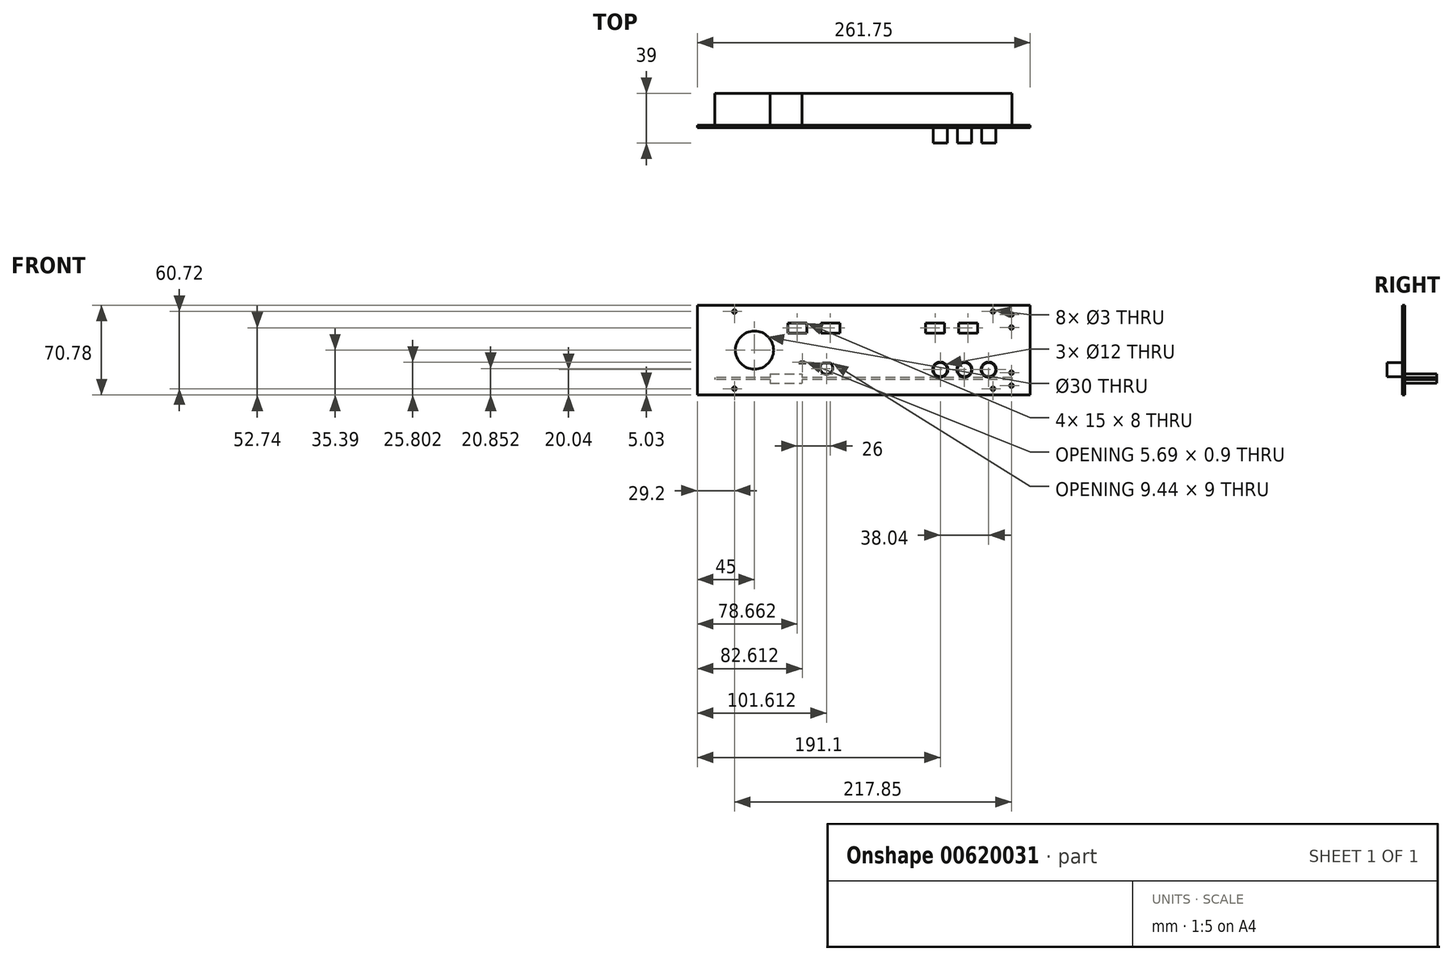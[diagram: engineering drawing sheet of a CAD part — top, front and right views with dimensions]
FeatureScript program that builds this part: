
annotation { "Feature Type Name" : "Feature", "Feature Type Description" : "" }
export const myFeature = defineFeature(function(context is Context, id is Id, definition is map)
    precondition{}
    {
        {
            var Q0;
            Q0=qCreatedBy(makeId("Front.planeOp"),FACE);
            var sketch = newSketch(context, id + "F0", { "sketchPlane" : qUnion([Q0])});
            skLineSegment(sketch, "E0.bottom", {"start": v(0, 0) * mm, "end": v(261.75, 0) * mm});
            skLineSegment(sketch, "E0.top", {"start": v(0, 70.78) * mm, "end": v(261.75, 70.78) * mm});
            skLineSegment(sketch, "E0.left", {"start": v(0, 0) * mm, "end": v(0, 70.78) * mm});
            skLineSegment(sketch, "E0.right", {"start": v(261.75, 0) * mm, "end": v(261.75, 70.78) * mm});
            skCircle(sketch, "E1", {"center": v(29.2, 5.03) * mm, "radius": 1.5 * mm});
            skCircle(sketch, "E2", {"center": v(29.2, 65.75) * mm, "radius": 1.5 * mm});
            skCircle(sketch, "E3", {"center": v(232.55, 65.75) * mm, "radius": 1.5 * mm});
            skCircle(sketch, "E4", {"center": v(232.55, 5.03) * mm, "radius": 1.5 * mm});
            skSolve(sketch);
        }
        {
            var Q0;
            Q0 = qSketchRegion(id + "F0", true);
            extrude(context, id + "F1", {"entities" : qUnion([Q0]), "oppositeDirection" : true, "depth" : 2 * mm, "offsetDistance" : 25 * mm});
        }
        {
            var Q0;
            Q0=makeQuery(id+"F1.opExtrude","CAP_FACE",FACE,{"disambiguationData":[OSD([sQuery(id+"F0.wireOp",EDGE,"E0.bottom"),sQuery(id+"F0.wireOp",EDGE,"E0.top"),sQuery(id+"F0.wireOp",EDGE,"E0.left"),sQuery(id+"F0.wireOp",EDGE,"E0.right"),sQuery(id+"F0.wireOp",EDGE,"E1"),sQuery(id+"F0.wireOp",EDGE,"E2"),sQuery(id+"F0.wireOp",EDGE,"E3"),sQuery(id+"F0.wireOp",EDGE,"E4")])],"isStart":false});
            var sketch = newSketch(context, id + "F2", { "sketchPlane" : qUnion([Q0])});
            skLineSegment(sketch, "E5.bottom", {"start": v(-247.63, 13.86) * mm, "end": v(-13.67, 13.86) * mm});
            skLineSegment(sketch, "E5.top", {"start": v(-247.63, 12.26) * mm, "end": v(-13.67, 12.26) * mm});
            skLineSegment(sketch, "E5.left", {"start": v(-247.63, 13.86) * mm, "end": v(-247.63, 12.26) * mm});
            skLineSegment(sketch, "E5.right", {"start": v(-13.67, 13.86) * mm, "end": v(-13.67, 12.26) * mm});
            skSolve(sketch);
        }
        {
            var Q0;
            Q0 = qSketchRegion(id + "F2", true);
            extrude(context, id + "F3", {"entities" : qUnion([Q0]), "operationType" : NewBodyOperationType.ADD, "depth" : 25 * mm, "offsetDistance" : 25 * mm});
        }
        {
            var Q0;
            Q0=makeQuery(id+"F1.opExtrude","CAP_FACE",FACE,{"disambiguationData":[OSD([sQuery(id+"F0.wireOp",EDGE,"E0.bottom"),sQuery(id+"F0.wireOp",EDGE,"E0.top"),sQuery(id+"F0.wireOp",EDGE,"E0.left"),sQuery(id+"F0.wireOp",EDGE,"E0.right"),sQuery(id+"F0.wireOp",EDGE,"E1"),sQuery(id+"F0.wireOp",EDGE,"E2"),sQuery(id+"F0.wireOp",EDGE,"E3"),sQuery(id+"F0.wireOp",EDGE,"E4")])],"isStart":false});
            var sketch = newSketch(context, id + "F4", { "sketchPlane" : qUnion([Q0])});
            skLineSegment(sketch, "E6.bottom", {"start": v(-57.2, 16.76) * mm, "end": v(-82.2, 16.76) * mm});
            skLineSegment(sketch, "E6.top", {"start": v(-57.2, 9.36) * mm, "end": v(-82.2, 9.36) * mm});
            skLineSegment(sketch, "E6.left", {"start": v(-57.2, 16.76) * mm, "end": v(-57.2, 9.36) * mm});
            skLineSegment(sketch, "E6.right", {"start": v(-82.2, 16.76) * mm, "end": v(-82.2, 9.36) * mm});
            skSolve(sketch);
        }
        {
            var Q0;
            Q0 = qSketchRegion(id + "F4", true);
            extrude(context, id + "F5", {"entities" : qUnion([Q0]), "operationType" : NewBodyOperationType.ADD, "depth" : 25 * mm, "offsetDistance" : 25 * mm});
        }
        {
            var Q0;
            Q0=makeQuery(id+"F1.opExtrude","CAP_FACE",FACE,{"disambiguationData":[OSD([sQuery(id+"F0.wireOp",EDGE,"E0.bottom"),sQuery(id+"F0.wireOp",EDGE,"E0.top"),sQuery(id+"F0.wireOp",EDGE,"E0.left"),sQuery(id+"F0.wireOp",EDGE,"E0.right"),sQuery(id+"F0.wireOp",EDGE,"E1"),sQuery(id+"F0.wireOp",EDGE,"E2"),sQuery(id+"F0.wireOp",EDGE,"E3"),sQuery(id+"F0.wireOp",EDGE,"E4")])],"isStart":false});
            var sketch = newSketch(context, id + "F6", { "sketchPlane" : qUnion([Q0])});
            skCircle(sketch, "E7", {"center": v(-229.14, 20.04) * mm, "radius": 6 * mm});
            skCircle(sketch, "E8", {"center": v(-210.12, 20.04) * mm, "radius": 6 * mm});
            skCircle(sketch, "E9", {"center": v(-191.1, 20.04) * mm, "radius": 6 * mm});
            skSolve(sketch);
        }
        {
            var Q0;
            Q0 = qSketchRegion(id + "F6", true);
            extrude(context, id + "F7", {"entities" : qUnion([Q0]), "operationType" : NewBodyOperationType.REMOVE, "oppositeDirection" : true, "depth" : 25 * mm, "offsetDistance" : 25 * mm});
        }
        {
            var Q0;
            Q0=makeQuery(id+"F1.opExtrude","CAP_FACE",FACE,{"disambiguationData":[OSD([sQuery(id+"F0.wireOp",EDGE,"E0.bottom"),sQuery(id+"F0.wireOp",EDGE,"E0.top"),sQuery(id+"F0.wireOp",EDGE,"E0.left"),sQuery(id+"F0.wireOp",EDGE,"E0.right"),sQuery(id+"F0.wireOp",EDGE,"E1"),sQuery(id+"F0.wireOp",EDGE,"E2"),sQuery(id+"F0.wireOp",EDGE,"E3"),sQuery(id+"F0.wireOp",EDGE,"E4")])],"isStart":false});
            var sketch = newSketch(context, id + "F8", { "sketchPlane" : qUnion([Q0])});
            skCircle(sketch, "E10", {"center": v(-229.14, 20.04) * mm, "radius": 5.5 * mm});
            skCircle(sketch, "E11", {"center": v(-210.12, 20.04) * mm, "radius": 5.5 * mm});
            skCircle(sketch, "E12", {"center": v(-191.1, 20.04) * mm, "radius": 5.5 * mm});
            skSolve(sketch);
        }
        {
            var Q0;
            Q0 = qSketchRegion(id + "F8", true);
            extrude(context, id + "F9", {"entities" : qUnion([Q0]), "oppositeDirection" : true, "depth" : 14 * mm, "offsetDistance" : 25 * mm});
        }
        {
            var Q0;
            Q0=makeQuery(id+"F1.opExtrude","CAP_FACE",FACE,{"disambiguationData":[OSD([sQuery(id+"F0.wireOp",EDGE,"E0.bottom"),sQuery(id+"F0.wireOp",EDGE,"E0.top"),sQuery(id+"F0.wireOp",EDGE,"E0.left"),sQuery(id+"F0.wireOp",EDGE,"E0.right"),sQuery(id+"F0.wireOp",EDGE,"E1"),sQuery(id+"F0.wireOp",EDGE,"E2"),sQuery(id+"F0.wireOp",EDGE,"E3"),sQuery(id+"F0.wireOp",EDGE,"E4")])],"isStart":true});
            var sketch = newSketch(context, id + "F10", { "sketchPlane" : qUnion([Q0])});
            skCircle(sketch, "E13", {"center": v(247.05, 7.45) * mm, "radius": 1.5 * mm});
            skCircle(sketch, "E14", {"center": v(247.05, 17.6) * mm, "radius": 1.5 * mm});
            skCircle(sketch, "E15", {"center": v(247.05, 53.17) * mm, "radius": 1.5 * mm});
            skCircle(sketch, "E16", {"center": v(247.05, 63.33) * mm, "radius": 1.5 * mm});
            skSolve(sketch);
        }
        {
            var Q0;
            Q0 = qSketchRegion(id + "F10", true);
            extrude(context, id + "F11", {"entities" : qUnion([Q0]), "operationType" : NewBodyOperationType.REMOVE, "oppositeDirection" : true, "depth" : 25 * mm, "offsetDistance" : 25 * mm});
        }
        {
            var Q0;
            Q0=makeQuery(id+"F1.opExtrude","CAP_FACE",FACE,{"disambiguationData":[OSD([sQuery(id+"F0.wireOp",EDGE,"E0.bottom"),sQuery(id+"F0.wireOp",EDGE,"E0.top"),sQuery(id+"F0.wireOp",EDGE,"E0.left"),sQuery(id+"F0.wireOp",EDGE,"E0.right"),sQuery(id+"F0.wireOp",EDGE,"E1"),sQuery(id+"F0.wireOp",EDGE,"E2"),sQuery(id+"F0.wireOp",EDGE,"E3"),sQuery(id+"F0.wireOp",EDGE,"E4")])],"isStart":true});
            var sketch = newSketch(context, id + "F12", { "sketchPlane" : qUnion([Q0])});
            skCircle(sketch, "E17", {"center": v(45, 35.4) * mm, "radius": 15 * mm});
            skSolve(sketch);
        }
        {
            var Q0;
            Q0 = qSketchRegion(id + "F12", true);
            extrude(context, id + "F13", {"entities" : qUnion([Q0]), "operationType" : NewBodyOperationType.REMOVE, "oppositeDirection" : true, "depth" : 25 * mm, "offsetDistance" : 25 * mm});
        }
        {
            var Q0;
            Q0=makeQuery(id+"F1.opExtrude","CAP_FACE",FACE,{"disambiguationData":[OSD([sQuery(id+"F0.wireOp",EDGE,"E0.bottom"),sQuery(id+"F0.wireOp",EDGE,"E0.top"),sQuery(id+"F0.wireOp",EDGE,"E0.left"),sQuery(id+"F0.wireOp",EDGE,"E0.right"),sQuery(id+"F0.wireOp",EDGE,"E1"),sQuery(id+"F0.wireOp",EDGE,"E2"),sQuery(id+"F0.wireOp",EDGE,"E3"),sQuery(id+"F0.wireOp",EDGE,"E4")])],"isStart":true});
            var sketch = newSketch(context, id + "F14", { "sketchPlane" : qUnion([Q0])});
            skLineSegment(sketch, "E18.bottom", {"start": v(71.16, 56.74) * mm, "end": v(86.16, 56.74) * mm});
            skLineSegment(sketch, "E18.top", {"start": v(71.16, 48.74) * mm, "end": v(86.16, 48.74) * mm});
            skLineSegment(sketch, "E18.left", {"start": v(71.16, 56.74) * mm, "end": v(71.16, 48.74) * mm});
            skLineSegment(sketch, "E18.right", {"start": v(86.16, 56.74) * mm, "end": v(86.16, 48.74) * mm});
            skLineSegment(sketch, "E19.bottom", {"start": v(97.16, 48.74) * mm, "end": v(112.16, 48.74) * mm});
            skLineSegment(sketch, "E19.top", {"start": v(97.16, 56.74) * mm, "end": v(112.16, 56.74) * mm});
            skLineSegment(sketch, "E19.left", {"start": v(97.16, 48.74) * mm, "end": v(97.16, 56.74) * mm});
            skLineSegment(sketch, "E19.right", {"start": v(112.16, 48.74) * mm, "end": v(112.16, 56.74) * mm});
            skLineSegment(sketch, "E20.bottom", {"start": v(179.5, 48.74) * mm, "end": v(194.5, 48.74) * mm});
            skLineSegment(sketch, "E20.top", {"start": v(179.5, 56.74) * mm, "end": v(194.5, 56.74) * mm});
            skLineSegment(sketch, "E20.left", {"start": v(179.5, 48.74) * mm, "end": v(179.5, 56.74) * mm});
            skLineSegment(sketch, "E20.right", {"start": v(194.5, 48.74) * mm, "end": v(194.5, 56.74) * mm});
            skLineSegment(sketch, "E21.bottom", {"start": v(205.5, 48.74) * mm, "end": v(220.5, 48.74) * mm});
            skLineSegment(sketch, "E21.top", {"start": v(205.5, 56.74) * mm, "end": v(220.5, 56.74) * mm});
            skLineSegment(sketch, "E21.left", {"start": v(205.5, 48.74) * mm, "end": v(205.5, 56.74) * mm});
            skLineSegment(sketch, "E21.right", {"start": v(220.5, 48.74) * mm, "end": v(220.5, 56.74) * mm});
            skSolve(sketch);
        }
        {
            var Q0;
            Q0 = qSketchRegion(id + "F14", true);
            extrude(context, id + "F15", {"entities" : qUnion([Q0]), "operationType" : NewBodyOperationType.REMOVE, "oppositeDirection" : true, "depth" : 25 * mm, "offsetDistance" : 25 * mm});
        }
        {
            var Q0;
            Q0=makeQuery(id+"F1.opExtrude","CAP_FACE",FACE,{"disambiguationData":[OSD([sQuery(id+"F0.wireOp",EDGE,"E0.bottom"),sQuery(id+"F0.wireOp",EDGE,"E0.top"),sQuery(id+"F0.wireOp",EDGE,"E0.left"),sQuery(id+"F0.wireOp",EDGE,"E0.right"),sQuery(id+"F0.wireOp",EDGE,"E1"),sQuery(id+"F0.wireOp",EDGE,"E2"),sQuery(id+"F0.wireOp",EDGE,"E3"),sQuery(id+"F0.wireOp",EDGE,"E4")])],"isStart":true});
            var sketch = newSketch(context, id + "F16", { "sketchPlane" : qUnion([Q0])});
            skCircle(sketch, "E22", {"center": v(82.61, 21.3) * mm, "radius": 4.95 * mm});
            skCircle(sketch, "E23", {"center": v(101.61, 21.3) * mm, "radius": 4.95 * mm});
            skLineSegment(sketch, "E24", {"start": v(75.99, 25.35) * mm, "end": v(113.83, 25.35) * mm});
            skSolve(sketch);
        }
        {
            var Q0;
            {var subQ0=sQuery(id+"F16.wireOp",EDGE,"E24");var subQ1=sQuery(id+"F16.wireOp",EDGE,"E22");var subQ2=makeQuery(id+"F16.imprint","INTERSECT",VERTEX,{"disambiguationData":[OD(0.0)],"derivedFrom":[subQ1,subQ0]});Q0=makeQuery(id+"F16.imprint","IMPRINT",FACE,{"disambiguationData":[TD([[makeQuery(id+"F16.imprint","IMPRINT",EDGE,{"disambiguationData":[TD([[subQ2,-1.0]])],"derivedFrom":subQ1}),1.0]])]});}
            var Q1;
            {var subQ0=sQuery(id+"F16.wireOp",EDGE,"E24");var subQ1=sQuery(id+"F16.wireOp",EDGE,"E23");var subQ2=makeQuery(id+"F16.imprint","INTERSECT",VERTEX,{"disambiguationData":[OD(0.0)],"derivedFrom":[subQ1,subQ0]});Q1=makeQuery(id+"F16.imprint","IMPRINT",FACE,{"disambiguationData":[TD([[makeQuery(id+"F16.imprint","IMPRINT",EDGE,{"disambiguationData":[TD([[subQ2,-1.0]])],"derivedFrom":subQ1}),1.0]])]});}
            extrude(context, id + "F17", {"entities" : qUnion([Q0, Q1]), "operationType" : NewBodyOperationType.REMOVE, "oppositeDirection" : true, "depth" : 25 * mm, "offsetDistance" : 25 * mm});
        }
    });
